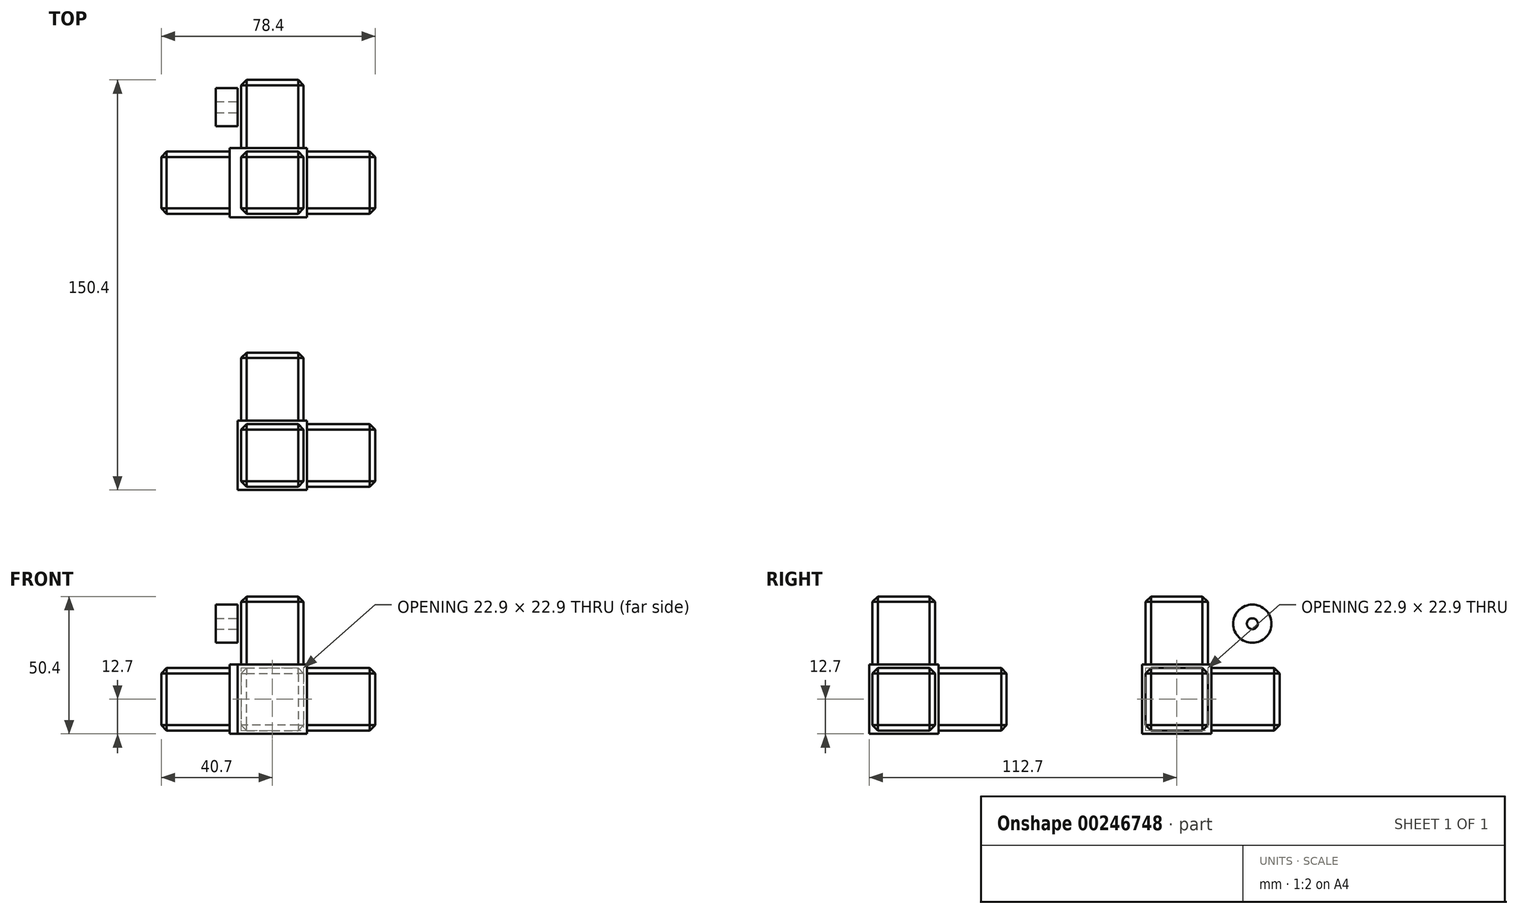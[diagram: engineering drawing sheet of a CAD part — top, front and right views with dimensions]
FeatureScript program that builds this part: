
annotation { "Feature Type Name" : "Feature", "Feature Type Description" : "" }
export const myFeature = defineFeature(function(context is Context, id is Id, definition is map)
    precondition{}
    {
        {
            var Q0;
            Q0=qCreatedBy(makeId("Top.planeOp"),FACE);
            var sketch = newSketch(context, id + "F0", { "sketchPlane" : qUnion([Q0])});
            skLineSegment(sketch, "E0.bottom", {"start": v(0, 0) * mm, "end": v(25.4, 0) * mm});
            skLineSegment(sketch, "E0.top", {"start": v(0, 25.4) * mm, "end": v(25.4, 25.4) * mm});
            skLineSegment(sketch, "E0.left", {"start": v(0, 0) * mm, "end": v(0, 25.4) * mm});
            skLineSegment(sketch, "E0.right", {"start": v(25.4, 0) * mm, "end": v(25.4, 25.4) * mm});
            skSolve(sketch);
        }
        {
            var Q0;
            Q0=makeQuery(id+"F0.imprint","IMPRINT",FACE,{"disambiguationData":[TD([[makeQuery(id+"F0.imprint","IMPRINT",EDGE,{"derivedFrom":sQuery(id+"F0.wireOp",EDGE,"E0.bottom")}),1.0]])]});
            extrude(context, id + "F1", {"entities" : qUnion([Q0]), "depth" : 25.4 * mm});
        }
        {
            var Q0;
            Q0=makeQuery(id+"F1.opExtrude","CAP_FACE",FACE,{"disambiguationData":[OSD([sQuery(id+"F0.wireOp",EDGE,"E0.bottom"),sQuery(id+"F0.wireOp",EDGE,"E0.top"),sQuery(id+"F0.wireOp",EDGE,"E0.left"),sQuery(id+"F0.wireOp",EDGE,"E0.right")])],"isStart":false});
            var sketch = newSketch(context, id + "F2", { "sketchPlane" : qUnion([Q0])});
            skLineSegment(sketch, "E1", {"start": v(25.4, 25.4) * mm, "end": v(0, 0) * mm, "construction": true});
            skLineSegment(sketch, "E2", {"start": v(0, 25.4) * mm, "end": v(25.4, 0) * mm, "construction": true});
            skLineSegment(sketch, "E3.bottom", {"start": v(1.25, 24.15) * mm, "end": v(24.15, 24.15) * mm});
            skLineSegment(sketch, "E3.top", {"start": v(1.25, 1.25) * mm, "end": v(24.15, 1.25) * mm});
            skLineSegment(sketch, "E3.left", {"start": v(1.25, 24.15) * mm, "end": v(1.25, 1.25) * mm});
            skLineSegment(sketch, "E3.right", {"start": v(24.15, 24.15) * mm, "end": v(24.15, 1.25) * mm});
            skPoint(sketch, "E3.middle", {"position": v(12.7, 12.7) * mm});
            skSolve(sketch);
        }
        {
            var Q0;
            Q0 = qSketchRegion(id + "F2", true);
            extrude(context, id + "F3", {"entities" : qUnion([Q0]), "operationType" : NewBodyOperationType.ADD, "depth" : 25 * mm});
        }
        {
            var Q0;
            Q0=makeQuery(id+"F1.opExtrude","SWEPT_FACE",FACE,{"disambiguationData":[OSD([sQuery(id+"F0.wireOp",EDGE,"E0.right")])]});
            var sketch = newSketch(context, id + "F4", { "sketchPlane" : qUnion([Q0])});
            skLineSegment(sketch, "E4", {"start": v(25.4, 25.4) * mm, "end": v(0, 0) * mm, "construction": true});
            skLineSegment(sketch, "E5", {"start": v(25.4, 0) * mm, "end": v(0, 25.4) * mm, "construction": true});
            skLineSegment(sketch, "E6.bottom", {"start": v(1.25, 24.15) * mm, "end": v(24.15, 24.15) * mm});
            skLineSegment(sketch, "E6.top", {"start": v(1.25, 1.25) * mm, "end": v(24.15, 1.25) * mm});
            skLineSegment(sketch, "E6.left", {"start": v(1.25, 24.15) * mm, "end": v(1.25, 1.25) * mm});
            skLineSegment(sketch, "E6.right", {"start": v(24.15, 24.15) * mm, "end": v(24.15, 1.25) * mm});
            skPoint(sketch, "E6.middle", {"position": v(12.7, 12.7) * mm});
            skSolve(sketch);
        }
        {
            var Q0;
            Q0 = qSketchRegion(id + "F4", true);
            extrude(context, id + "F5", {"entities" : qUnion([Q0]), "operationType" : NewBodyOperationType.ADD, "depth" : 25 * mm});
        }
        {
            var Q0;
            Q0=makeQuery(id+"F1.opExtrude","SWEPT_FACE",FACE,{"disambiguationData":[OSD([sQuery(id+"F0.wireOp",EDGE,"E0.top")])]});
            var sketch = newSketch(context, id + "F6", { "sketchPlane" : qUnion([Q0])});
            skLineSegment(sketch, "E7", {"start": v(-25.4, 0) * mm, "end": v(0, 25.4) * mm, "construction": true});
            skLineSegment(sketch, "E8", {"start": v(0, 0) * mm, "end": v(-25.4, 25.4) * mm, "construction": true});
            skLineSegment(sketch, "E9.bottom", {"start": v(-1.25, 24.15) * mm, "end": v(-24.15, 24.15) * mm});
            skLineSegment(sketch, "E9.top", {"start": v(-1.25, 1.25) * mm, "end": v(-24.15, 1.25) * mm});
            skLineSegment(sketch, "E9.left", {"start": v(-1.25, 24.15) * mm, "end": v(-1.25, 1.25) * mm});
            skLineSegment(sketch, "E9.right", {"start": v(-24.15, 24.15) * mm, "end": v(-24.15, 1.25) * mm});
            skPoint(sketch, "E9.middle", {"position": v(-12.7, 12.7) * mm});
            skSolve(sketch);
        }
        {
            var Q0;
            Q0=makeQuery(id+"F6.imprint","IMPRINT",FACE,{"disambiguationData":[TD([[makeQuery(id+"F6.imprint","IMPRINT",EDGE,{"derivedFrom":sQuery(id+"F6.wireOp",EDGE,"E9.bottom")}),1.0]])]});
            extrude(context, id + "F7", {"entities" : qUnion([Q0]), "operationType" : NewBodyOperationType.ADD, "depth" : 25 * mm});
        }
        {
            var Q0;
            Q0=makeQuery(id+"F3.opExtrude","CAP_FACE",FACE,{"disambiguationData":[OSD([sQuery(id+"F2.wireOp",EDGE,"E3.bottom"),sQuery(id+"F2.wireOp",EDGE,"E3.top"),sQuery(id+"F2.wireOp",EDGE,"E3.left"),sQuery(id+"F2.wireOp",EDGE,"E3.right")])],"isStart":false});
            var Q1;
            Q1=makeQuery(id+"F3.opExtrude","SWEPT_EDGE",EDGE,{"disambiguationData":[OSD([sQuery(id+"F2.wireOp",EDGE,"E3.top"),sQuery(id+"F2.wireOp",EDGE,"E3.left")])]});
            var Q2;
            Q2=makeQuery(id+"F3.opExtrude","SWEPT_EDGE",EDGE,{"disambiguationData":[OSD([sQuery(id+"F2.wireOp",EDGE,"E3.top"),sQuery(id+"F2.wireOp",EDGE,"E3.right")])]});
            var Q3;
            Q3=makeQuery(id+"F3.opExtrude","SWEPT_EDGE",EDGE,{"disambiguationData":[OSD([sQuery(id+"F2.wireOp",EDGE,"E3.bottom"),sQuery(id+"F2.wireOp",EDGE,"E3.left")])]});
            var Q4;
            Q4=makeQuery(id+"F3.opExtrude","SWEPT_EDGE",EDGE,{"disambiguationData":[OSD([sQuery(id+"F2.wireOp",EDGE,"E3.bottom"),sQuery(id+"F2.wireOp",EDGE,"E3.right")])]});
            var Q5;
            Q5=makeQuery(id+"F5.opExtrude","SWEPT_EDGE",EDGE,{"disambiguationData":[OSD([sQuery(id+"F4.wireOp",EDGE,"E6.top"),sQuery(id+"F4.wireOp",EDGE,"E6.left")])]});
            var Q6;
            Q6=makeQuery(id+"F5.opExtrude","SWEPT_EDGE",EDGE,{"disambiguationData":[OSD([sQuery(id+"F4.wireOp",EDGE,"E6.bottom"),sQuery(id+"F4.wireOp",EDGE,"E6.left")])]});
            var Q7;
            Q7=makeQuery(id+"F5.opExtrude","CAP_FACE",FACE,{"disambiguationData":[OSD([sQuery(id+"F4.wireOp",EDGE,"E6.bottom"),sQuery(id+"F4.wireOp",EDGE,"E6.top"),sQuery(id+"F4.wireOp",EDGE,"E6.left"),sQuery(id+"F4.wireOp",EDGE,"E6.right")])],"isStart":false});
            var Q8;
            Q8=makeQuery(id+"F5.opExtrude","SWEPT_EDGE",EDGE,{"disambiguationData":[OSD([sQuery(id+"F4.wireOp",EDGE,"E6.top"),sQuery(id+"F4.wireOp",EDGE,"E6.right")])]});
            var Q9;
            Q9=makeQuery(id+"F5.opExtrude","SWEPT_EDGE",EDGE,{"disambiguationData":[OSD([sQuery(id+"F4.wireOp",EDGE,"E6.bottom"),sQuery(id+"F4.wireOp",EDGE,"E6.right")])]});
            var Q10;
            Q10=makeQuery(id+"F7.opExtrude","CAP_FACE",FACE,{"disambiguationData":[OSD([sQuery(id+"F6.wireOp",EDGE,"E9.bottom"),sQuery(id+"F6.wireOp",EDGE,"E9.top"),sQuery(id+"F6.wireOp",EDGE,"E9.left"),sQuery(id+"F6.wireOp",EDGE,"E9.right")])],"isStart":false});
            var Q11;
            Q11=makeQuery(id+"F7.opExtrude","SWEPT_EDGE",EDGE,{"disambiguationData":[OSD([sQuery(id+"F6.wireOp",EDGE,"E9.bottom"),sQuery(id+"F6.wireOp",EDGE,"E9.right")])]});
            var Q12;
            Q12=makeQuery(id+"F7.opExtrude","SWEPT_EDGE",EDGE,{"disambiguationData":[OSD([sQuery(id+"F6.wireOp",EDGE,"E9.bottom"),sQuery(id+"F6.wireOp",EDGE,"E9.left")])]});
            var Q13;
            Q13=makeQuery(id+"F7.opExtrude","SWEPT_EDGE",EDGE,{"disambiguationData":[OSD([sQuery(id+"F6.wireOp",EDGE,"E9.top"),sQuery(id+"F6.wireOp",EDGE,"E9.right")])]});
            var Q14;
            Q14=makeQuery(id+"F7.opExtrude","SWEPT_EDGE",EDGE,{"disambiguationData":[OSD([sQuery(id+"F6.wireOp",EDGE,"E9.top"),sQuery(id+"F6.wireOp",EDGE,"E9.left")])]});
            chamfer(context, id + "F8", {"entities" : qUnion([Q0, Q1, Q2, Q3, Q4, Q5, Q6, Q7, Q8, Q9, Q10, Q11, Q12, Q13, Q14]), "width" : 2 * mm, "tangentPropagation" : true});
        }
        {
            var Q0;
            Q0=makeQuery(id+"F1.opExtrude","SWEPT_BODY",BODY,{"disambiguationData":[OSD([sQuery(id+"F0.wireOp",EDGE,"E0.bottom"),sQuery(id+"F0.wireOp",EDGE,"E0.top"),sQuery(id+"F0.wireOp",EDGE,"E0.left"),sQuery(id+"F0.wireOp",EDGE,"E0.right")])]});
            transform(context, id + "F9", {"entities" : qUnion([Q0]), "transformType" : TransformType.TRANSLATION_3D, "dx" : 150 * mm, "dy" : 0 * mm, "dz" : 0 * mm, "makeCopy" : true});
        }
        {
            var Q0;
            Q0=makeQuery(id+"F9.opPattern","COPY",BODY,{"derivedFrom":makeQuery(id+"F1.opExtrude","SWEPT_BODY",BODY,{"disambiguationData":[OSD([sQuery(id+"F0.wireOp",EDGE,"E0.bottom"),sQuery(id+"F0.wireOp",EDGE,"E0.top"),sQuery(id+"F0.wireOp",EDGE,"E0.left"),sQuery(id+"F0.wireOp",EDGE,"E0.right")])]}),"instanceName":"1"});
            deleteBodies(context, id + "F10", {"entities" : qUnion([Q0])});
        }
        {
            var Q0;
            Q0=makeQuery(id+"F1.opExtrude","SWEPT_BODY",BODY,{"disambiguationData":[OSD([sQuery(id+"F0.wireOp",EDGE,"E0.bottom"),sQuery(id+"F0.wireOp",EDGE,"E0.top"),sQuery(id+"F0.wireOp",EDGE,"E0.left"),sQuery(id+"F0.wireOp",EDGE,"E0.right")])]});
            transform(context, id + "F11", {"entities" : qUnion([Q0]), "transformType" : TransformType.TRANSLATION_3D, "dx" : 0 * mm, "dy" : 100 * mm, "dz" : 0 * mm, "makeCopy" : true});
        }
        {
            var Q0;
            Q0=makeQuery(id+"F11.opPattern","COPY",FACE,{"derivedFrom":makeQuery(id+"F1.opExtrude","SWEPT_FACE",FACE,{"disambiguationData":[OSD([sQuery(id+"F0.wireOp",EDGE,"E0.left")])]}),"instanceName":"1"});
            var sketch = newSketch(context, id + "F12", { "sketchPlane" : qUnion([Q0])});
            skLineSegment(sketch, "E10.bottom", {"start": v(-100, 0) * mm, "end": v(-150.4, 0) * mm});
            skLineSegment(sketch, "E10.top", {"start": v(-100, 50.4) * mm, "end": v(-140.4, 50.4) * mm});
            skLineSegment(sketch, "E10.left", {"start": v(-100, 0) * mm, "end": v(-100, 50.4) * mm});
            skLineSegment(sketch, "E10.right", {"start": v(-150.4, 0) * mm, "end": v(-150.4, 40.4) * mm});
            skLineSegment(sketch, "E11.bottom", {"start": v(-100, 0) * mm, "end": v(-125.4, 0) * mm});
            skLineSegment(sketch, "E11.top", {"start": v(-100, 25.4) * mm, "end": v(-125.4, 25.4) * mm});
            skLineSegment(sketch, "E11.left", {"start": v(-100, 0) * mm, "end": v(-100, 25.4) * mm});
            skLineSegment(sketch, "E11.right", {"start": v(-125.4, 0) * mm, "end": v(-125.4, 25.4) * mm});
            skPoint(sketch, "E12.visualSharp", {"position": v(-150.4, 50.4) * mm});
            skArc(sketch, "E12.filletArc", {"start": v(-140.4, 50.4) * mm, "mid": v(-147.47, 47.47) * mm, "end": v(-150.4, 40.4) * mm});
            skCircle(sketch, "E13", {"center": v(-140.4, 40.4) * mm, "radius": 2 * mm});
            skCircle(sketch, "E14", {"center": v(-140.4, 40.4) * mm, "radius": 7 * mm});
            skLineSegment(sketch, "E15", {"start": v(-100, 50.4) * mm, "end": v(-150.4, 0) * mm, "construction": true});
            skLineSegment(sketch, "E16", {"start": v(-100, 25.4) * mm, "end": v(-125, 50.4) * mm, "construction": true});
            skLineSegment(sketch, "E17", {"start": v(-125.4, 0) * mm, "end": v(-150.8, 25.4) * mm, "construction": true});
            skCircle(sketch, "E18", {"center": v(-137.9, 12.5) * mm, "radius": 2.15 * mm});
            skCircle(sketch, "E19", {"center": v(-112.5, 37.9) * mm, "radius": 2.15 * mm});
            skSolve(sketch);
        }
        {
            var Q0;
            Q0=makeQuery(id+"F12.imprint","IMPRINT",FACE,{"disambiguationData":[TD([[makeQuery(id+"F12.imprint","IMPRINT",EDGE,{"derivedFrom":sQuery(id+"F12.wireOp",EDGE,"E11.bottom")}),-1.0]])]});
            var Q1;
            Q1=makeQuery(id+"F12.imprint","IMPRINT",FACE,{"disambiguationData":[TD([[makeQuery(id+"F12.imprint","IMPRINT",EDGE,{"derivedFrom":sQuery(id+"F12.wireOp",EDGE,"E10.bottom")}),-1.0]])]});
            extrude(context, id + "F13", {"entities" : qUnion([Q0, Q1]), "operationType" : NewBodyOperationType.ADD, "depth" : 3 * mm});
        }
        {
            var Q0;
            Q0=makeQuery(id+"F12.imprint","IMPRINT",FACE,{"disambiguationData":[TD([[makeQuery(id+"F12.imprint","IMPRINT",EDGE,{"derivedFrom":sQuery(id+"F12.wireOp",EDGE,"E13")}),-1.0]])]});
            extrude(context, id + "F14", {"entities" : qUnion([Q0]), "operationType" : NewBodyOperationType.ADD, "depth" : 8 * mm});
        }
        {
            var Q0;
            Q0=makeQuery(id+"F13.opExtrude","CAP_FACE",FACE,{"disambiguationData":[OSD([sQuery(id+"F12.wireOp",EDGE,"E10.bottom"),sQuery(id+"F12.wireOp",EDGE,"E10.top"),sQuery(id+"F12.wireOp",EDGE,"E10.left"),sQuery(id+"F12.wireOp",EDGE,"E10.right"),sQuery(id+"F12.wireOp",EDGE,"E11.bottom"),sQuery(id+"F12.wireOp",EDGE,"E11.left"),sQuery(id+"F12.wireOp",EDGE,"E12.filletArc"),sQuery(id+"F12.wireOp",EDGE,"E14"),sQuery(id+"F12.wireOp",EDGE,"E18"),sQuery(id+"F12.wireOp",EDGE,"E19")])],"isStart":false});
            var sketch = newSketch(context, id + "F15", { "sketchPlane" : qUnion([Q0])});
            skLineSegment(sketch, "E20.bottom", {"start": v(-100, 0) * mm, "end": v(-125.4, 0) * mm, "construction": true});
            skLineSegment(sketch, "E20.top", {"start": v(-100, 25.4) * mm, "end": v(-125.4, 25.4) * mm, "construction": true});
            skLineSegment(sketch, "E20.left", {"start": v(-100, 0) * mm, "end": v(-100, 25.4) * mm, "construction": true});
            skLineSegment(sketch, "E20.right", {"start": v(-125.4, 0) * mm, "end": v(-125.4, 25.4) * mm, "construction": true});
            skLineSegment(sketch, "E21", {"start": v(-125.4, 25.4) * mm, "end": v(-100, 0) * mm, "construction": true});
            skLineSegment(sketch, "E22", {"start": v(-100, 25.4) * mm, "end": v(-125.4, 0) * mm, "construction": true});
            skLineSegment(sketch, "E23.bottom", {"start": v(-124.15, 1.25) * mm, "end": v(-101.25, 1.25) * mm});
            skLineSegment(sketch, "E23.top", {"start": v(-124.15, 24.15) * mm, "end": v(-101.25, 24.15) * mm});
            skLineSegment(sketch, "E23.left", {"start": v(-124.15, 1.25) * mm, "end": v(-124.15, 24.15) * mm});
            skLineSegment(sketch, "E23.right", {"start": v(-101.25, 1.25) * mm, "end": v(-101.25, 24.15) * mm});
            skPoint(sketch, "E23.middle", {"position": v(-112.7, 12.7) * mm});
            skSolve(sketch);
        }
        {
            var Q0;
            Q0=makeQuery(id+"F15.imprint","IMPRINT",FACE,{"disambiguationData":[TD([[makeQuery(id+"F15.imprint","IMPRINT",EDGE,{"derivedFrom":sQuery(id+"F15.wireOp",EDGE,"E23.bottom")}),1.0]])]});
            extrude(context, id + "F16", {"entities" : qUnion([Q0]), "operationType" : NewBodyOperationType.ADD, "depth" : 25 * mm});
        }
        {
            var Q0;
            Q0=makeQuery(id+"F16.opExtrude","SWEPT_EDGE",EDGE,{"disambiguationData":[OSD([sQuery(id+"F15.wireOp",EDGE,"E23.top"),sQuery(id+"F15.wireOp",EDGE,"E23.left")])]});
            var Q1;
            Q1=makeQuery(id+"F16.opExtrude","SWEPT_EDGE",EDGE,{"disambiguationData":[OSD([sQuery(id+"F15.wireOp",EDGE,"E23.bottom"),sQuery(id+"F15.wireOp",EDGE,"E23.left")])]});
            var Q2;
            Q2=makeQuery(id+"F16.opExtrude","CAP_EDGE",EDGE,{"disambiguationData":[OSD([sQuery(id+"F15.wireOp",EDGE,"E23.left")])],"isStart":false});
            var Q3;
            Q3=makeQuery(id+"F16.opExtrude","CAP_EDGE",EDGE,{"disambiguationData":[OSD([sQuery(id+"F15.wireOp",EDGE,"E23.right")])],"isStart":false});
            var Q4;
            Q4=makeQuery(id+"F16.opExtrude","CAP_EDGE",EDGE,{"disambiguationData":[OSD([sQuery(id+"F15.wireOp",EDGE,"E23.top")])],"isStart":false});
            var Q5;
            Q5=makeQuery(id+"F16.opExtrude","CAP_EDGE",EDGE,{"disambiguationData":[OSD([sQuery(id+"F15.wireOp",EDGE,"E23.bottom")])],"isStart":false});
            var Q6;
            Q6=makeQuery(id+"F16.opExtrude","SWEPT_EDGE",EDGE,{"disambiguationData":[OSD([sQuery(id+"F15.wireOp",EDGE,"E23.top"),sQuery(id+"F15.wireOp",EDGE,"E23.right")])]});
            var Q7;
            Q7=makeQuery(id+"F16.opExtrude","SWEPT_EDGE",EDGE,{"disambiguationData":[OSD([sQuery(id+"F15.wireOp",EDGE,"E23.bottom"),sQuery(id+"F15.wireOp",EDGE,"E23.right")])]});
            chamfer(context, id + "F17", {"entities" : qUnion([Q0, Q1, Q2, Q3, Q4, Q5, Q6, Q7]), "width" : 2 * mm, "tangentPropagation" : true});
        }
    });
